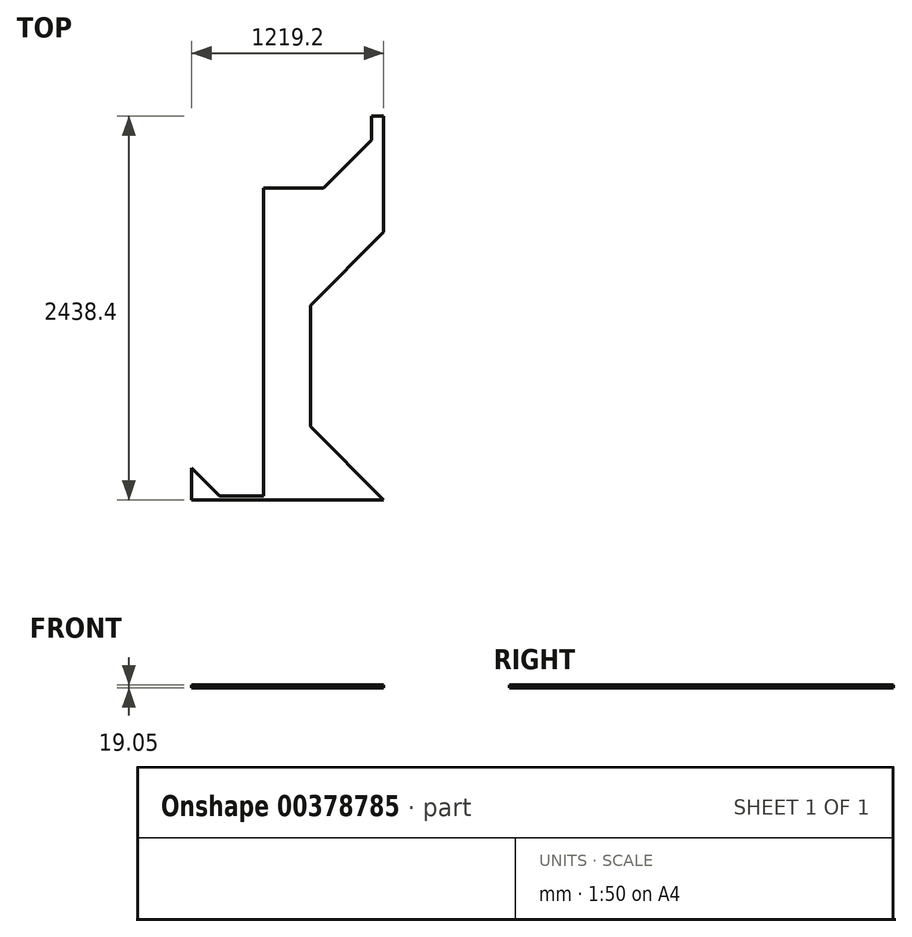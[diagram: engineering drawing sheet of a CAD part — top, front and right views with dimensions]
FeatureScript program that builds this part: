
annotation { "Feature Type Name" : "Feature", "Feature Type Description" : "" }
export const myFeature = defineFeature(function(context is Context, id is Id, definition is map)
    precondition{}
    {
        {
            var Q0;
            Q0=qCreatedBy(makeId("Top.planeOp"),FACE);
            var sketch = newSketch(context, id + "F0", { "sketchPlane" : qUnion([Q0])});
            skLineSegment(sketch, "E0.bottom", {"start": v(-42.57, 2374.17) * mm, "end": v(1176.63, 2374.17) * mm});
            skLineSegment(sketch, "E0.top", {"start": v(-42.57, -64.23) * mm, "end": v(1176.63, -64.23) * mm});
            skLineSegment(sketch, "E0.left", {"start": v(-42.57, 2374.17) * mm, "end": v(-42.57, -64.23) * mm});
            skLineSegment(sketch, "E0.right", {"start": v(1176.63, 2374.17) * mm, "end": v(1176.63, -64.23) * mm});
            skSolve(sketch);
        }
        {
            var Q0;
            Q0 = qSketchRegion(id + "F0", true);
            extrude(context, id + "F1", {"entities" : qUnion([Q0]), "oppositeDirection" : true, "depth" : 19.05 * mm});
        }
        {
            var Q0;
            Q0=makeQuery(id+"F1.opExtrude","CAP_FACE",FACE,{"disambiguationData":[OSD([sQuery(id+"F0.wireOp",EDGE,"E0.bottom"),sQuery(id+"F0.wireOp",EDGE,"E0.top"),sQuery(id+"F0.wireOp",EDGE,"E0.left"),sQuery(id+"F0.wireOp",EDGE,"E0.right")])],"isStart":true});
            var sketch = newSketch(context, id + "F2", { "sketchPlane" : qUnion([Q0])});
            skLineSegment(sketch, "E1", {"start": v(-42.57, 2374.17) * mm, "end": v(414.63, 1916.97) * mm});
            skLineSegment(sketch, "E2", {"start": v(414.63, 1916.97) * mm, "end": v(414.63, 1129.57) * mm});
            skLineSegment(sketch, "E3", {"start": v(414.63, 1129.57) * mm, "end": v(-42.57, 672.37) * mm});
            skLineSegment(sketch, "E4", {"start": v(-42.57, 672.37) * mm, "end": v(-42.57, 2374.17) * mm});
            skSolve(sketch);
        }
        {
            var Q0;
            Q0 = qSketchRegion(id + "F2", true);
            extrude(context, id + "F3", {"entities" : qUnion([Q0]), "operationType" : NewBodyOperationType.REMOVE, "oppositeDirection" : true, "depth" : 25.4 * mm});
        }
        {
            var Q0;
            Q0=makeQuery(id+"F1.opExtrude","CAP_FACE",FACE,{"disambiguationData":[OSD([sQuery(id+"F0.wireOp",EDGE,"E0.bottom"),sQuery(id+"F0.wireOp",EDGE,"E0.top"),sQuery(id+"F0.wireOp",EDGE,"E0.left"),sQuery(id+"F0.wireOp",EDGE,"E0.right")])],"isStart":true});
            var sketch = newSketch(context, id + "F4", { "sketchPlane" : qUnion([Q0])});
            skLineSegment(sketch, "E5", {"start": v(-42.57, 672.37) * mm, "end": v(414.63, 1129.57) * mm});
            skLineSegment(sketch, "E6", {"start": v(414.63, 1129.57) * mm, "end": v(414.63, -38.83) * mm});
            skLineSegment(sketch, "E7", {"start": v(-42.57, 672.37) * mm, "end": v(-42.57, 138.97) * mm});
            skLineSegment(sketch, "E8", {"start": v(-42.57, 138.97) * mm, "end": v(135.23, -38.83) * mm});
            skLineSegment(sketch, "E9", {"start": v(135.23, -38.83) * mm, "end": v(414.63, -38.83) * mm});
            skSolve(sketch);
        }
        {
            var Q0;
            Q0 = qSketchRegion(id + "F4", true);
            extrude(context, id + "F5", {"entities" : qUnion([Q0]), "operationType" : NewBodyOperationType.REMOVE, "oppositeDirection" : true, "depth" : 25.4 * mm});
        }
        {
            var Q0;
            Q0=makeQuery(id+"F1.opExtrude","CAP_FACE",FACE,{"disambiguationData":[OSD([sQuery(id+"F0.wireOp",EDGE,"E0.bottom"),sQuery(id+"F0.wireOp",EDGE,"E0.top"),sQuery(id+"F0.wireOp",EDGE,"E0.left"),sQuery(id+"F0.wireOp",EDGE,"E0.right")])],"isStart":true});
            var sketch = newSketch(context, id + "F6", { "sketchPlane" : qUnion([Q0])});
            skLineSegment(sketch, "E10", {"start": v(414.63, 1916.97) * mm, "end": v(795.63, 1916.97) * mm});
            skLineSegment(sketch, "E11", {"start": v(795.63, 1916.97) * mm, "end": v(1100.43, 2221.77) * mm});
            skLineSegment(sketch, "E12", {"start": v(1100.43, 2221.77) * mm, "end": v(1100.43, 2374.17) * mm});
            skLineSegment(sketch, "E13", {"start": v(1100.43, 2374.17) * mm, "end": v(-42.57, 2374.17) * mm});
            skLineSegment(sketch, "E14", {"start": v(-42.57, 2374.17) * mm, "end": v(414.63, 1916.97) * mm});
            skSolve(sketch);
        }
        {
            var Q0;
            Q0 = qSketchRegion(id + "F6", true);
            extrude(context, id + "F7", {"entities" : qUnion([Q0]), "operationType" : NewBodyOperationType.REMOVE, "oppositeDirection" : true, "depth" : 25.4 * mm});
        }
        {
            var Q0;
            Q0=makeQuery(id+"F1.opExtrude","CAP_FACE",FACE,{"disambiguationData":[OSD([sQuery(id+"F0.wireOp",EDGE,"E0.bottom"),sQuery(id+"F0.wireOp",EDGE,"E0.top"),sQuery(id+"F0.wireOp",EDGE,"E0.left"),sQuery(id+"F0.wireOp",EDGE,"E0.right")])],"isStart":true});
            var sketch = newSketch(context, id + "F8", { "sketchPlane" : qUnion([Q0])});
            skLineSegment(sketch, "E15", {"start": v(1176.63, -64.23) * mm, "end": v(710.56, 401.84) * mm});
            skLineSegment(sketch, "E16", {"start": v(710.56, 401.84) * mm, "end": v(710.56, 1171.5) * mm});
            skLineSegment(sketch, "E17", {"start": v(710.56, 1171.5) * mm, "end": v(1176.63, 1637.57) * mm});
            skLineSegment(sketch, "E18", {"start": v(1176.63, 1637.57) * mm, "end": v(1176.63, -64.23) * mm});
            skSolve(sketch);
        }
        {
            var Q0;
            Q0 = qSketchRegion(id + "F8", true);
            extrude(context, id + "F9", {"entities" : qUnion([Q0]), "operationType" : NewBodyOperationType.REMOVE, "oppositeDirection" : true, "depth" : 25.4 * mm});
        }
    });
